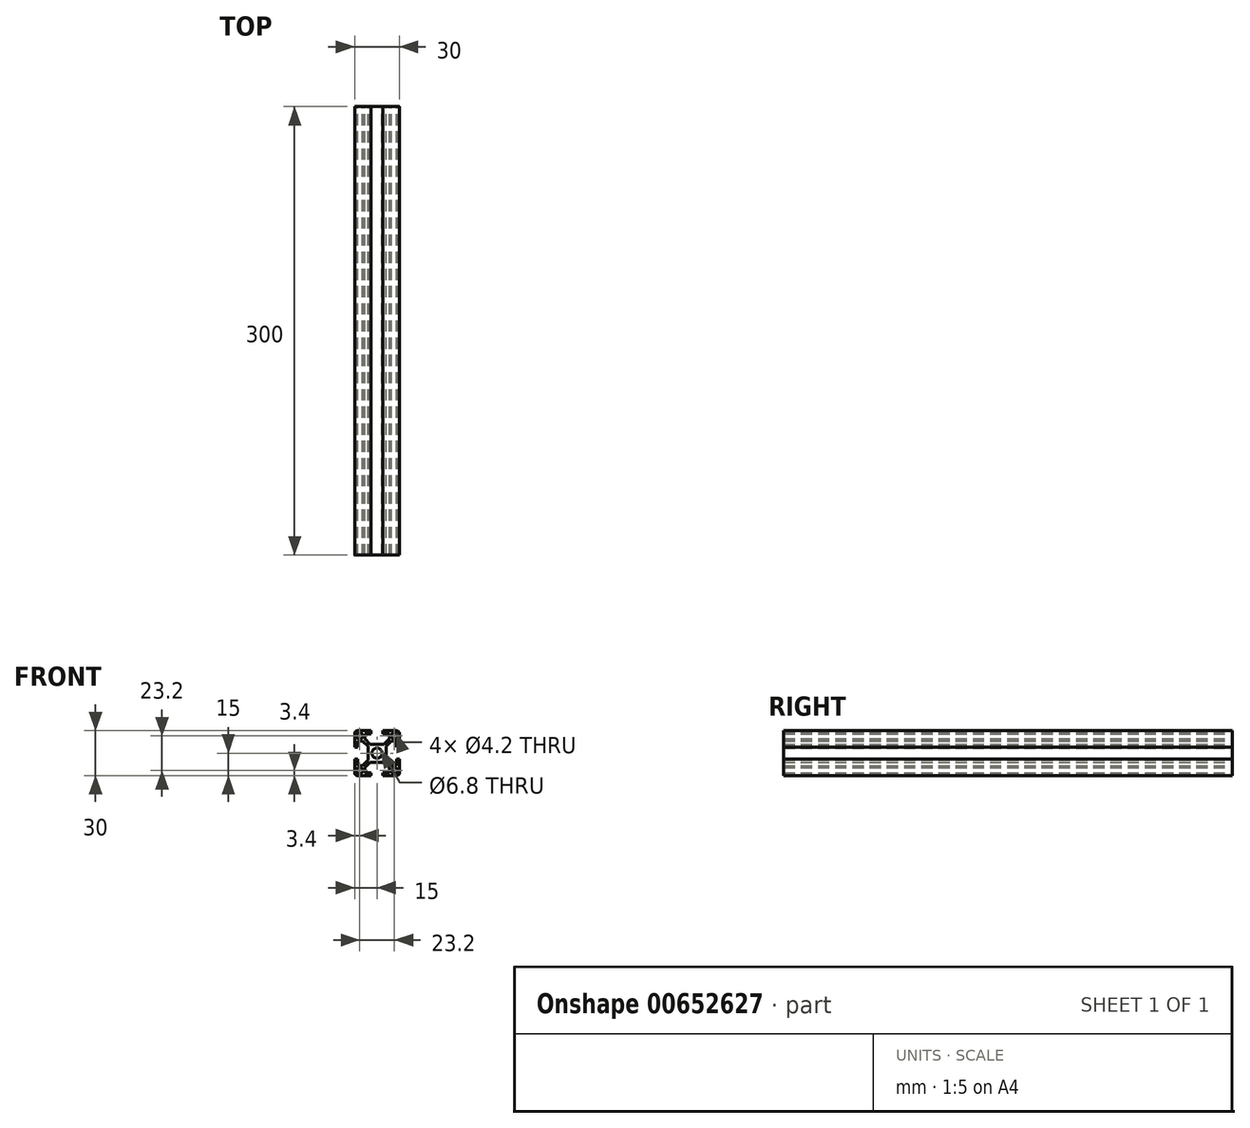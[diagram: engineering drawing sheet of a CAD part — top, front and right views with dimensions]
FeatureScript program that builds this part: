
annotation { "Feature Type Name" : "Feature", "Feature Type Description" : "" }
export const myFeature = defineFeature(function(context is Context, id is Id, definition is map)
    precondition{}
    {
        {
            var Q0;
            Q0=qCreatedBy(makeId("Front.planeOp"),FACE);
            var sketch = newSketch(context, id + "F0", { "sketchPlane" : qUnion([Q0])});
            skLineSegment(sketch, "E0", {"start": v(0, 6) * mm, "end": v(-4.59, 6) * mm});
            skLineSegment(sketch, "E1", {"start": v(-4.59, 6) * mm, "end": v(-8.25, 9.66) * mm});
            skLineSegment(sketch, "E2", {"start": v(-8.25, 9.66) * mm, "end": v(-8.25, 13) * mm});
            skLineSegment(sketch, "E3", {"start": v(-8.25, 13) * mm, "end": v(-4, 13) * mm});
            skLineSegment(sketch, "E4", {"start": v(-4, 13) * mm, "end": v(-4, 15) * mm});
            skLineSegment(sketch, "E5", {"start": v(-4, 15) * mm, "end": v(-13, 15) * mm});
            skLineSegment(sketch, "E6", {"start": v(-15, 13) * mm, "end": v(-15, 4) * mm});
            skLineSegment(sketch, "E7", {"start": v(-15, 4) * mm, "end": v(-13, 4) * mm});
            skLineSegment(sketch, "E8", {"start": v(-13, 4) * mm, "end": v(-13, 8.25) * mm});
            skLineSegment(sketch, "E9", {"start": v(-13, 8.25) * mm, "end": v(-9.66, 8.25) * mm});
            skLineSegment(sketch, "E10", {"start": v(-9.66, 8.25) * mm, "end": v(-6, 4.59) * mm});
            skLineSegment(sketch, "E11", {"start": v(-6, 4.59) * mm, "end": v(-6, 0) * mm});
            skLineSegment(sketch, "E12", {"start": v(-6, 0) * mm, "end": v(0, 0) * mm, "construction": true});
            skLineSegment(sketch, "E13", {"start": v(0, 0) * mm, "end": v(0, 6) * mm, "construction": true});
            skArc(sketch, "E14", {"start": v(0, 3.4) * mm, "mid": v(-2.4, 2.4) * mm, "end": v(-3.4, 0) * mm});
            skCircle(sketch, "E15", {"center": v(-11.6, 11.6) * mm, "radius": 2.1 * mm});
            skLineSegment(sketch, "E16", {"start": v(0, 0) * mm, "end": v(-7.38, 7.38) * mm, "construction": true});
            skLineSegment(sketch, "E17.1.0", {"start": v(-8.25, -13) * mm, "end": v(-8.25, -9.66) * mm});
            skLineSegment(sketch, "E17.1.1", {"start": v(-4, -15) * mm, "end": v(-4, -13) * mm});
            skLineSegment(sketch, "E17.1.2", {"start": v(-4, -13) * mm, "end": v(-8.25, -13) * mm});
            skLineSegment(sketch, "E17.1.3", {"start": v(-15, -4) * mm, "end": v(-15, -13) * mm});
            skLineSegment(sketch, "E17.1.4", {"start": v(-8.25, -9.66) * mm, "end": v(-4.59, -6) * mm});
            skLineSegment(sketch, "E17.1.5", {"start": v(-13, -15) * mm, "end": v(-4, -15) * mm});
            skLineSegment(sketch, "E17.1.6", {"start": v(-4.59, -6) * mm, "end": v(0, -6) * mm});
            skLineSegment(sketch, "E17.1.7", {"start": v(0, -6) * mm, "end": v(0, 0) * mm, "construction": true});
            skLineSegment(sketch, "E17.1.8", {"start": v(0, 0) * mm, "end": v(-6, 0) * mm, "construction": true});
            skLineSegment(sketch, "E17.1.9", {"start": v(-13, -4) * mm, "end": v(-15, -4) * mm});
            skLineSegment(sketch, "E17.1.10", {"start": v(-13, -8.25) * mm, "end": v(-13, -4) * mm});
            skArc(sketch, "E17.1.11", {"start": v(-3.4, 0) * mm, "mid": v(-2.4, -2.4) * mm, "end": v(0, -3.4) * mm});
            skLineSegment(sketch, "E17.1.12", {"start": v(-9.66, -8.25) * mm, "end": v(-13, -8.25) * mm});
            skLineSegment(sketch, "E17.1.13", {"start": v(0, 0) * mm, "end": v(-7.38, -7.38) * mm, "construction": true});
            skLineSegment(sketch, "E17.1.14", {"start": v(-6, -4.59) * mm, "end": v(-9.66, -8.25) * mm});
            skCircle(sketch, "E17.1.15", {"center": v(-11.6, -11.6) * mm, "radius": 2.1 * mm});
            skLineSegment(sketch, "E17.1.16", {"start": v(-6, 0) * mm, "end": v(-6, -4.59) * mm});
            skLineSegment(sketch, "E17.2.0", {"start": v(13, -8.25) * mm, "end": v(9.66, -8.25) * mm});
            skLineSegment(sketch, "E17.2.1", {"start": v(15, -4) * mm, "end": v(13, -4) * mm});
            skLineSegment(sketch, "E17.2.2", {"start": v(13, -4) * mm, "end": v(13, -8.25) * mm});
            skLineSegment(sketch, "E17.2.3", {"start": v(4, -15) * mm, "end": v(13, -15) * mm});
            skLineSegment(sketch, "E17.2.4", {"start": v(9.66, -8.25) * mm, "end": v(6, -4.59) * mm});
            skLineSegment(sketch, "E17.2.5", {"start": v(15, -13) * mm, "end": v(15, -4) * mm});
            skLineSegment(sketch, "E17.2.6", {"start": v(6, -4.59) * mm, "end": v(6, 0) * mm});
            skLineSegment(sketch, "E17.2.7", {"start": v(6, 0) * mm, "end": v(0, 0) * mm, "construction": true});
            skLineSegment(sketch, "E17.2.8", {"start": v(0, 0) * mm, "end": v(0, -6) * mm, "construction": true});
            skLineSegment(sketch, "E17.2.9", {"start": v(4, -13) * mm, "end": v(4, -15) * mm});
            skLineSegment(sketch, "E17.2.10", {"start": v(8.25, -13) * mm, "end": v(4, -13) * mm});
            skArc(sketch, "E17.2.11", {"start": v(0, -3.4) * mm, "mid": v(2.4, -2.4) * mm, "end": v(3.4, 0) * mm});
            skLineSegment(sketch, "E17.2.12", {"start": v(8.25, -9.66) * mm, "end": v(8.25, -13) * mm});
            skLineSegment(sketch, "E17.2.13", {"start": v(0, 0) * mm, "end": v(7.38, -7.38) * mm, "construction": true});
            skLineSegment(sketch, "E17.2.14", {"start": v(4.59, -6) * mm, "end": v(8.25, -9.66) * mm});
            skCircle(sketch, "E17.2.15", {"center": v(11.6, -11.6) * mm, "radius": 2.1 * mm});
            skLineSegment(sketch, "E17.2.16", {"start": v(0, -6) * mm, "end": v(4.59, -6) * mm});
            skLineSegment(sketch, "E17.3.0", {"start": v(8.25, 13) * mm, "end": v(8.25, 9.66) * mm});
            skLineSegment(sketch, "E17.3.1", {"start": v(4, 15) * mm, "end": v(4, 13) * mm});
            skLineSegment(sketch, "E17.3.2", {"start": v(4, 13) * mm, "end": v(8.25, 13) * mm});
            skLineSegment(sketch, "E17.3.3", {"start": v(15, 4) * mm, "end": v(15, 13) * mm});
            skLineSegment(sketch, "E17.3.4", {"start": v(8.25, 9.66) * mm, "end": v(4.59, 6) * mm});
            skLineSegment(sketch, "E17.3.5", {"start": v(13, 15) * mm, "end": v(4, 15) * mm});
            skLineSegment(sketch, "E17.3.6", {"start": v(4.59, 6) * mm, "end": v(0, 6) * mm});
            skLineSegment(sketch, "E17.3.7", {"start": v(0, 6) * mm, "end": v(0, 0) * mm, "construction": true});
            skLineSegment(sketch, "E17.3.8", {"start": v(0, 0) * mm, "end": v(6, 0) * mm, "construction": true});
            skLineSegment(sketch, "E17.3.9", {"start": v(13, 4) * mm, "end": v(15, 4) * mm});
            skLineSegment(sketch, "E17.3.10", {"start": v(13, 8.25) * mm, "end": v(13, 4) * mm});
            skArc(sketch, "E17.3.11", {"start": v(3.4, 0) * mm, "mid": v(2.4, 2.4) * mm, "end": v(0, 3.4) * mm});
            skLineSegment(sketch, "E17.3.12", {"start": v(9.66, 8.25) * mm, "end": v(13, 8.25) * mm});
            skLineSegment(sketch, "E17.3.13", {"start": v(0, 0) * mm, "end": v(7.38, 7.38) * mm, "construction": true});
            skLineSegment(sketch, "E17.3.14", {"start": v(6, 4.59) * mm, "end": v(9.66, 8.25) * mm});
            skCircle(sketch, "E17.3.15", {"center": v(11.6, 11.6) * mm, "radius": 2.1 * mm});
            skLineSegment(sketch, "E17.3.16", {"start": v(6, 0) * mm, "end": v(6, 4.59) * mm});
            skPoint(sketch, "E18.visualSharp", {"position": v(-15, 15) * mm});
            skArc(sketch, "E18.filletArc", {"start": v(-13, 15) * mm, "mid": v(-14.41, 14.41) * mm, "end": v(-15, 13) * mm});
            skPoint(sketch, "E19.visualSharp", {"position": v(15, 15) * mm});
            skArc(sketch, "E19.filletArc", {"start": v(15, 13) * mm, "mid": v(14.41, 14.41) * mm, "end": v(13, 15) * mm});
            skPoint(sketch, "E20.visualSharp", {"position": v(15, -15) * mm});
            skArc(sketch, "E20.filletArc", {"start": v(13, -15) * mm, "mid": v(14.41, -14.41) * mm, "end": v(15, -13) * mm});
            skPoint(sketch, "E21.visualSharp", {"position": v(-15, -15) * mm});
            skArc(sketch, "E21.filletArc", {"start": v(-15, -13) * mm, "mid": v(-14.41, -14.41) * mm, "end": v(-13, -15) * mm});
            skSolve(sketch);
        }
        {
            var Q0;
            Q0 = qSketchRegion(id + "F0", true);
            extrude(context, id + "F1", {"entities" : qUnion([Q0]), "depth" : 300 * mm, "offsetDistance" : 25 * mm});
        }
    });
